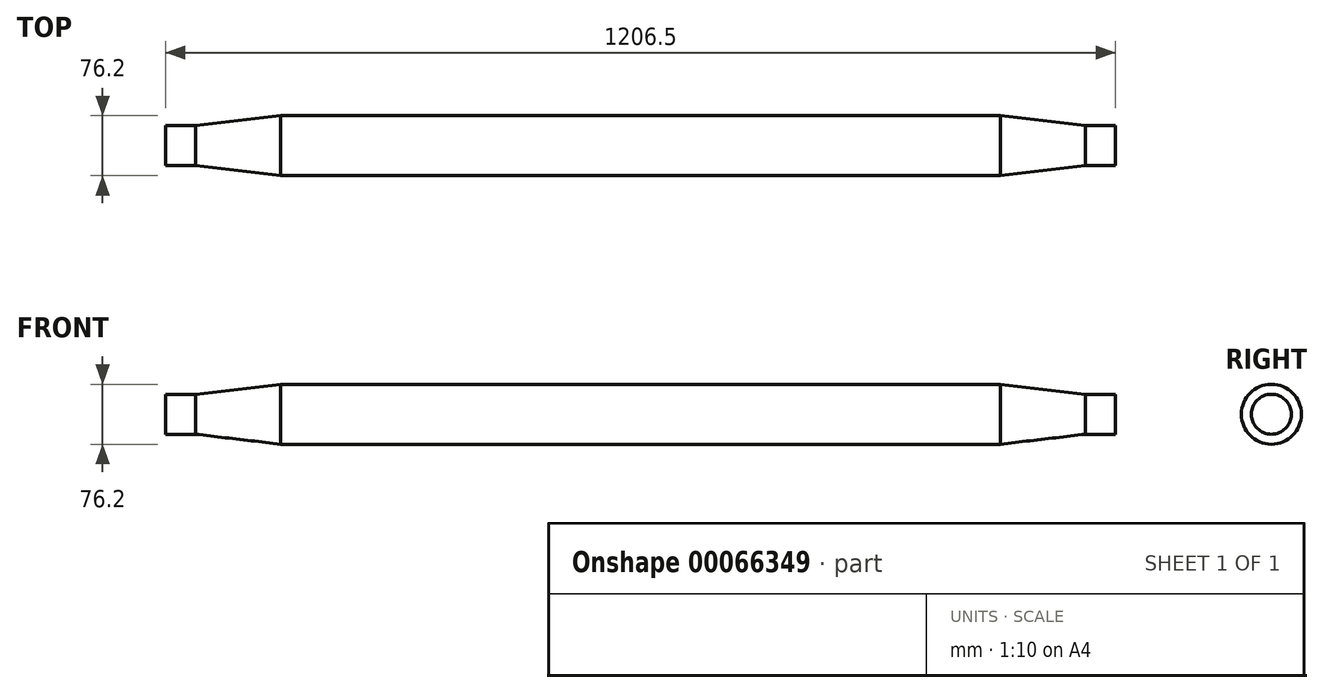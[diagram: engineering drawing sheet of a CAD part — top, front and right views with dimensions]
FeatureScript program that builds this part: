
annotation { "Feature Type Name" : "Feature", "Feature Type Description" : "" }
export const myFeature = defineFeature(function(context is Context, id is Id, definition is map)
    precondition{}
    {
        {
            var Q0;
            Q0=qCreatedBy(makeId("Right.planeOp"),FACE);
            var sketch = newSketch(context, id + "F0", { "sketchPlane" : qUnion([Q0])});
            skCircle(sketch, "E0", {"center": v(0, 0) * mm, "radius": 38.1 * mm});
            skSolve(sketch);
        }
        {
            var Q0;
            Q0=qSketchRegion(id+"F0",true);
            extrude(context, id + "F1", {"entities" : qUnion([Q0]), "endBound" : BoundingType.SYMMETRIC, "depth" : 914.4 * mm});
        }
        {
            var Q0;
            Q0=makeQuery(id+"F1.opExtrude","CAP_FACE",FACE,{"disambiguationData":[OSD([sQuery(id+"F0.wireOp",EDGE,"E0")])],"isStart":false});
            cPlane(context, id + "F2", {"entities" : qUnion([Q0]), "cplaneType" : CPlaneType.OFFSET, "offset" : 107.95 * mm, "width" : 152.4 * mm, "height" : 152.4 * mm});
        }
        {
            var Q0;
            Q0=qCreatedBy(id+"F2.planeOp",FACE);
            var sketch = newSketch(context, id + "F3", { "sketchPlane" : qUnion([Q0])});
            skCircle(sketch, "E1", {"center": v(0, 0) * mm, "radius": 25.4 * mm});
            skSolve(sketch);
        }
        {
            var Q0;
            Q0=qSketchRegion(id+"F3",true);
            extrude(context, id + "F4", {"entities" : qUnion([Q0]), "depth" : 38.1 * mm});
        }
        {
            var Q0;
            Q0=makeQuery(id+"F1.opExtrude","CAP_FACE",FACE,{"disambiguationData":[OSD([sQuery(id+"F0.wireOp",EDGE,"E0")])],"isStart":false});
            var Q1;
            Q1=makeQuery(id+"F4.opExtrude","CAP_FACE",FACE,{"disambiguationData":[OSD([sQuery(id+"F3.wireOp",EDGE,"E1")])],"isStart":true});
            loft(context, id + "F5", {"sheetProfilesArray" : [{ "sheetProfileEntities" : qUnion([Q0]) }, { "sheetProfileEntities" : qUnion([Q1]) }]});
        }
        {
            var Q0;
            Q0=makeQuery(id+"F4.opExtrude","SWEPT_BODY",BODY,{"disambiguationData":[OSD([sQuery(id+"F3.wireOp",EDGE,"E1")])]});
            var Q1;
            Q1=makeQuery(id+"F5.opLoft","SWEPT_BODY",BODY,{"disambiguationData":[OSD([sQuery(id+"F0.wireOp",EDGE,"E0"),sQuery(id+"F3.wireOp",EDGE,"E1")])]});
            var Q2;
            Q2=qCreatedBy(makeId("Right.planeOp"),FACE);
            mirror(context, id + "F6", {"operationType" : NewBodyOperationType.ADD, "entities" : qUnion([Q0, Q1]), "mirrorPlane" : qUnion([Q2])});
        }
    });
